# Revit family: Sanitary_Bath-And-Spas_Sanindusa_Easy-Bathtub
name_source: partatom
category: Plumbing Fixtures
revit_build: Autodesk Revit 2018 (Build: 20170223_1515(x64)
units: mm (PartAtom-declared; Revit-internal decimal feet)

## family parameters
Always vertical = Yes
Cut with Voids When Loaded = No
OmniClass Number = 23.45.00.00
OmniClass Title = Sanitary, Laundry, and Cleaning Equipment
Part Type = Normal
Room Calculation Point = No
Round Connector Dimension = Use Diameter
Shared = No
Work Plane-Based = No

## types (1)
- Sanitary_Bath-And-Spas_Sanindusa_Easy-Bathtub
    AssetType = Fixed
    BarCode = 5604815439021
    CodePerformance = EN 14527:2006 / A1:2010
CL 2
    Color = white
    Constituents = ref.490-50 automatic pop up waste for bathtub(not included); ref.811-70 fix kit feets for bathtub(not included); ref.800202-75 Panel(not included); ref. 805801-170 vertice panel(not included)
    Cost = 0 $
    Description = Sanitary appliance for immersion of the human body or parts of it (BS6100)
    DrainSize = 52 mm
    Edition number = 1
    Element Type = BATH: Sanitary appliance for immersion of the human body or parts of it (BS6100)
    Features = Bathtub for residential or hotel solution. Range with various sizes available. Symmetrical bathtub with valve to the center.
    Finish = gloss
    Installation Instructions = https://www.tec.sanindusa.pt
    InstallationDate = 1900-12-31T23:59:59
    ManufacturerName = Sanindusa
    ManufacturerURL = www.tec.sanindusa.pt
    Material = 3.2 mm acrylic sheet reinforced with polyester resin, fiberglass and 16 mm wood agglomerate on the bottom
    ModelNumber = 8069000000
    ModelReference = Easy
    Name = Bathtub easy 170x75
    NominalHeight = 416 mm
    NominalLength = 1700 mm  [stored 5.57743 ft]
    NominalWidth = 750 mm  [stored 2.46063 ft]
    Pre-defined type (IFC) = BATH
    Product Guid = 3b90dc0f-f408-4ac5-8c2d-0aee8c1b839a
    Product data url = https://bimobject.com
    ProductInformation = https://www.tec.sanindusa.pt
    ProductionYear = 2018
    Shape = Rectangular
    Size = 1700x750
    Type (IFC) = IfcSanitaryTerminalType
    URL = www.tec.sanindusa.pt
    Uniclass2015Code = Ss_​40_​15_​75_​05
    Uniclass2015Title = Bath systems
    Uniclass2015Version = Systems v1.9
    Version = 1
    WarrantyDescription = https://www.tec.sanindusa.pt
    WarrantyDurationParts = 5
    WarrantyDurationUnit = year
    WarrantyStartDate = 1900-12-31T23:59:59
1900-12-31T23:59:59
    Weight = 21.50 kg

note: [stored X ft] marks values corroborated as IEEE doubles in the binary element streams (Revit-internal decimal feet)

## geometry (parser evidence)
native form markers: Sweep x7
no freeform markers — native parametric forms only
